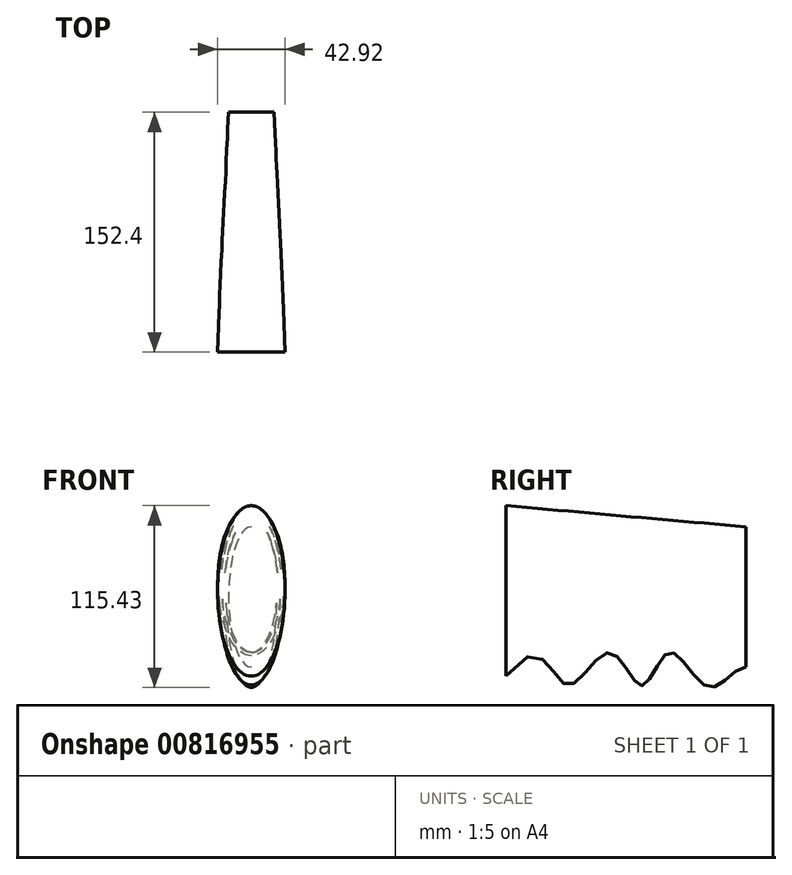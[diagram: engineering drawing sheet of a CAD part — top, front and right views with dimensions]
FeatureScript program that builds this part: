
annotation { "Feature Type Name" : "Feature", "Feature Type Description" : "" }
export const myFeature = defineFeature(function(context is Context, id is Id, definition is map)
    precondition{}
    {
        {
            var Q0;
            Q0=qCreatedBy(makeId("Front.planeOp"),FACE);
            var sketch = newSketch(context, id + "F0", { "sketchPlane" : qUnion([Q0])});
            skEllipse(sketch, "E0", {"center": v(0, -3.83) * mm, "majorRadius": 44.48 * mm, "minorRadius": 14.47 * mm, "majorAxis": v(0, 1)});
            skPoint(sketch, "E1", {"position": v(0, 40.65) * mm});
            skPoint(sketch, "E2", {"position": v(0, -48.32) * mm});
            skSolve(sketch);
        }
        {
            var Q0;
            Q0=qCreatedBy(makeId("Front.planeOp"),FACE);
            cPlane(context, id + "F1", {"entities" : qUnion([Q0]), "cplaneType" : CPlaneType.OFFSET, "offset" : 152.4 * mm, "width" : 152.4 * mm, "height" : 152.4 * mm});
        }
        {
            var Q0;
            Q0=qCreatedBy(id+"F1.planeOp",FACE);
            var sketch = newSketch(context, id + "F2", { "sketchPlane" : qUnion([Q0])});
            skEllipse(sketch, "E3", {"center": v(0, 0) * mm, "majorRadius": 54.15 * mm, "minorRadius": 21.46 * mm, "majorAxis": v(0, 1)});
            skPoint(sketch, "E4", {"position": v(0, 54.15) * mm});
            skPoint(sketch, "E5", {"position": v(0, -54.15) * mm});
            skSolve(sketch);
        }
        {
            var Q0;
            Q0=qCreatedBy(makeId("Right.planeOp"),FACE);
            var sketch = newSketch(context, id + "F3", { "sketchPlane" : qUnion([Q0])});
            skFitSpline(sketch, "E6", {"points": [v(0, 40.65) * mm, v(-152.4, 54.15) * mm], "startDerivative": vector(-151.7, 13.5) * mm, "endDerivative": vector(-151.7, 13.5) * mm});
            skFitSpline(sketch, "E7", {"points": [v(-152.4, -54.15) * mm, v(-114.4, -59.61) * mm, v(-86.78, -39.06) * mm, v(-66.23, -60.23) * mm, v(-48.43, -39.06) * mm, v(-23.58, -61.15) * mm, v(0, -48.32) * mm], "startDerivative": vector(368.68, 501.21) * mm, "endDerivative": vector(152.93, 5.52) * mm});
            skSolve(sketch);
        }
        {
            var Q0;
            Q0=makeQuery(id+"F2.imprint","IMPRINT",FACE,{"disambiguationData":[TD([[makeQuery(id+"F2.imprint","IMPRINT",EDGE,{"derivedFrom":sQuery(id+"F2.wireOp",EDGE,"E3")}),1.0]])]});
            var Q1;
            Q1=makeQuery(id+"F0.imprint","IMPRINT",FACE,{"disambiguationData":[TD([[makeQuery(id+"F0.imprint","IMPRINT",EDGE,{"derivedFrom":sQuery(id+"F0.wireOp",EDGE,"E0")}),1.0]])]});
            var Q2;
            Q2=sQuery(id+"F3.wireOp",EDGE,"E7");
            var Q3;
            Q3=sQuery(id+"F3.wireOp",EDGE,"E6");
            loft(context, id + "F4", {"addGuides" : true, "sheetProfilesArray" : [{ "sheetProfileEntities" : qUnion([Q0]) }, { "sheetProfileEntities" : qUnion([Q1]) }], "guidesArray" : [{ "guideEntities" : qUnion([Q2]), "guideDerivativeType" : LoftGuideDerivativeType.DEFAULT, "guideDerivativeMagnitude" : 1 }, { "guideEntities" : qUnion([Q3]), "guideDerivativeType" : LoftGuideDerivativeType.DEFAULT, "guideDerivativeMagnitude" : 1 }]});
        }
    });
